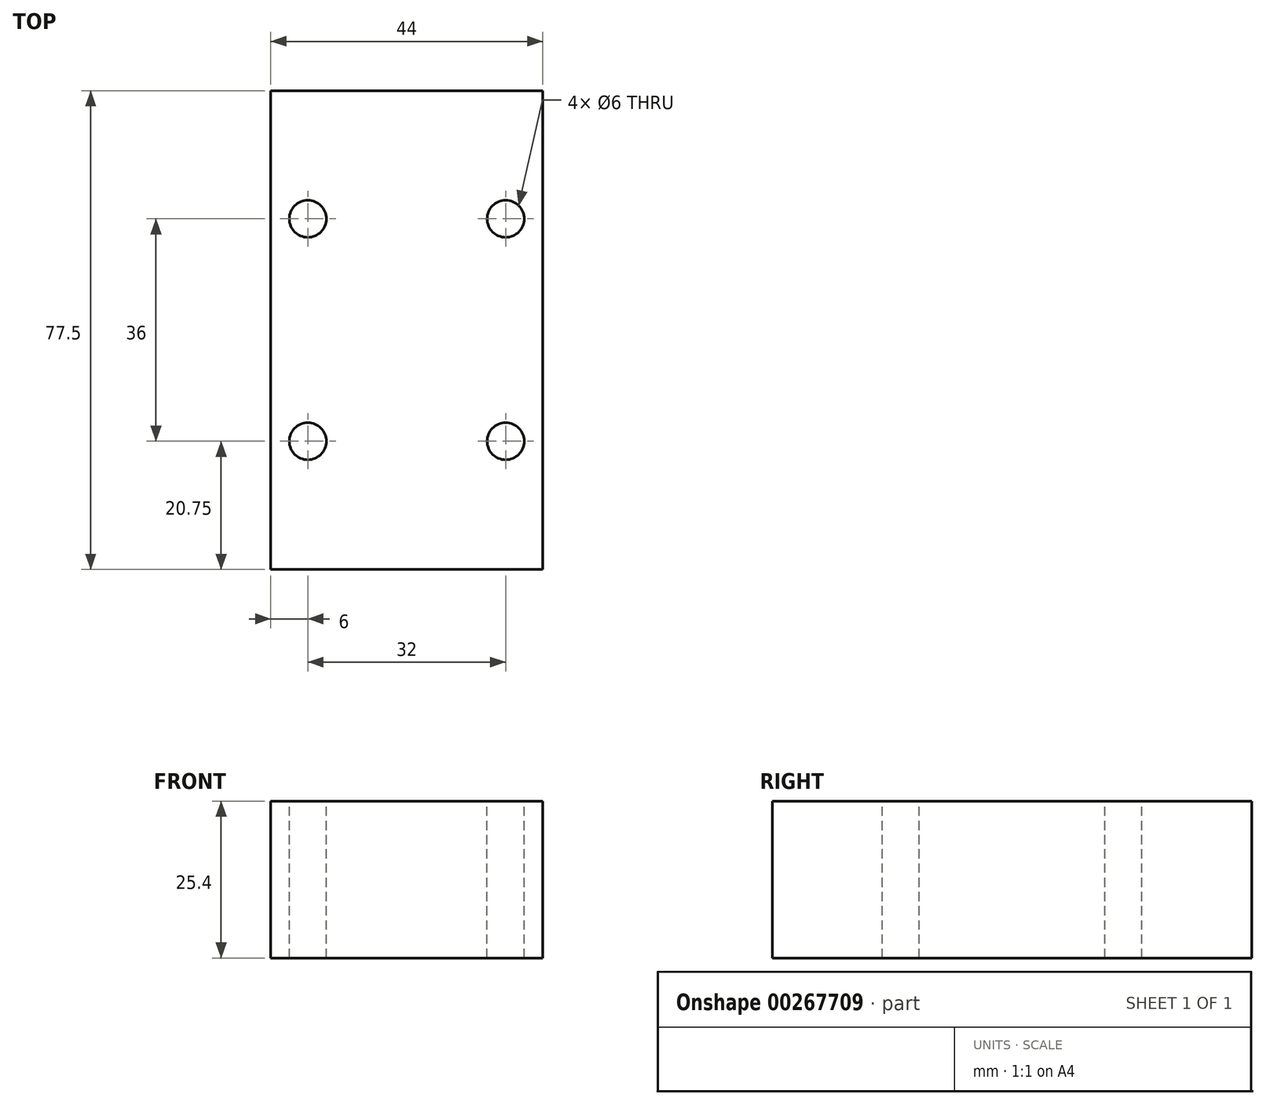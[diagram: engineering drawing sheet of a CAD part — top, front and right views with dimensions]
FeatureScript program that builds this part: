
annotation { "Feature Type Name" : "Feature", "Feature Type Description" : "" }
export const myFeature = defineFeature(function(context is Context, id is Id, definition is map)
    precondition{}
    {
        {
            var Q0;
            Q0=qCreatedBy(makeId("Front.planeOp"),FACE);
            var sketch = newSketch(context, id + "F0", { "sketchPlane" : qUnion([Q0])});
            skLineSegment(sketch, "E0.bottom", {"start": v(-22, 12.7) * mm, "end": v(22, 12.7) * mm});
            skLineSegment(sketch, "E0.top", {"start": v(-22, -12.7) * mm, "end": v(22, -12.7) * mm});
            skLineSegment(sketch, "E0.left", {"start": v(-22, 12.7) * mm, "end": v(-22, -12.7) * mm});
            skLineSegment(sketch, "E0.right", {"start": v(22, 12.7) * mm, "end": v(22, -12.7) * mm});
            skPoint(sketch, "E0.middle", {"position": v(0, 0) * mm});
            skSolve(sketch);
        }
        {
            var Q0;
            Q0 = qSketchRegion(id + "F0", true);
            extrude(context, id + "F1", {"entities" : qUnion([Q0]), "oppositeDirection" : true, "depth" : 77.5 * mm});
        }
        {
            var Q0;
            Q0=makeQuery(id+"F1.opExtrude","SWEPT_FACE",FACE,{"disambiguationData":[OSD([sQuery(id+"F0.wireOp",EDGE,"E0.bottom")])]});
            var sketch = newSketch(context, id + "F2", { "sketchPlane" : qUnion([Q0])});
            skLineSegment(sketch, "E1.bottom", {"start": v(16, 118.22) * mm, "end": v(-16, 118.22) * mm, "construction": true});
            skLineSegment(sketch, "E1.top", {"start": v(16, -118.22) * mm, "end": v(-16, -118.22) * mm, "construction": true});
            skLineSegment(sketch, "E1.left", {"start": v(16, 118.22) * mm, "end": v(16, -118.22) * mm, "construction": true});
            skLineSegment(sketch, "E1.right", {"start": v(-16, 118.22) * mm, "end": v(-16, -118.22) * mm, "construction": true});
            skPoint(sketch, "E1.middle", {"position": v(0, 0) * mm});
            skLineSegment(sketch, "E2", {"start": v(-22, 38.75) * mm, "end": v(22, 38.75) * mm, "construction": true});
            skLineSegment(sketch, "E3.bottom", {"start": v(16, 56.75) * mm, "end": v(-25.34, 56.75) * mm, "construction": true});
            skLineSegment(sketch, "E3.top", {"start": v(16, 20.75) * mm, "end": v(-25.34, 20.75) * mm, "construction": true});
            skLineSegment(sketch, "E3.right", {"start": v(-25.34, 56.75) * mm, "end": v(-25.34, 20.75) * mm, "construction": true});
            skPoint(sketch, "E3.middle", {"position": v(-4.67, 38.75) * mm});
            skCircle(sketch, "E4", {"center": v(-16, 56.75) * mm, "radius": 3 * mm});
            skCircle(sketch, "E5", {"center": v(16, 56.75) * mm, "radius": 3 * mm});
            skCircle(sketch, "E6", {"center": v(-16, 20.75) * mm, "radius": 3 * mm});
            skCircle(sketch, "E7", {"center": v(16, 20.75) * mm, "radius": 3 * mm});
            skSolve(sketch);
        }
        {
            var Q0;
            Q0=makeQuery(id+"F2.imprint","IMPRINT",FACE,{"disambiguationData":[TD([[makeQuery(id+"F2.imprint","IMPRINT",EDGE,{"derivedFrom":sQuery(id+"F2.wireOp",EDGE,"E4")}),1.0]])]});
            var Q1;
            Q1=makeQuery(id+"F2.imprint","IMPRINT",FACE,{"disambiguationData":[TD([[makeQuery(id+"F2.imprint","IMPRINT",EDGE,{"derivedFrom":sQuery(id+"F2.wireOp",EDGE,"E6")}),1.0]])]});
            var Q2;
            Q2=makeQuery(id+"F2.imprint","IMPRINT",FACE,{"disambiguationData":[TD([[makeQuery(id+"F2.imprint","IMPRINT",EDGE,{"derivedFrom":sQuery(id+"F2.wireOp",EDGE,"E7")}),1.0]])]});
            var Q3;
            Q3=makeQuery(id+"F2.imprint","IMPRINT",FACE,{"disambiguationData":[TD([[makeQuery(id+"F2.imprint","IMPRINT",EDGE,{"derivedFrom":sQuery(id+"F2.wireOp",EDGE,"E5")}),1.0]])]});
            var Q4;
            Q4=sQuery(id+"F2.wireOp",EDGE,"E4");
            var Q5;
            Q5=sQuery(id+"F2.wireOp",EDGE,"E6");
            var Q6;
            Q6=sQuery(id+"F2.wireOp",EDGE,"E7");
            var Q7;
            Q7=sQuery(id+"F2.wireOp",EDGE,"E5");
            extrude(context, id + "F3", {"entities" : qUnion([Q0, Q1, Q2, Q3]), "operationType" : NewBodyOperationType.REMOVE, "surfaceEntities" : qUnion([Q4, Q5, Q6, Q7]), "endBound" : BoundingType.THROUGH_ALL, "oppositeDirection" : true, "depth" : 25 * mm});
        }
    });
